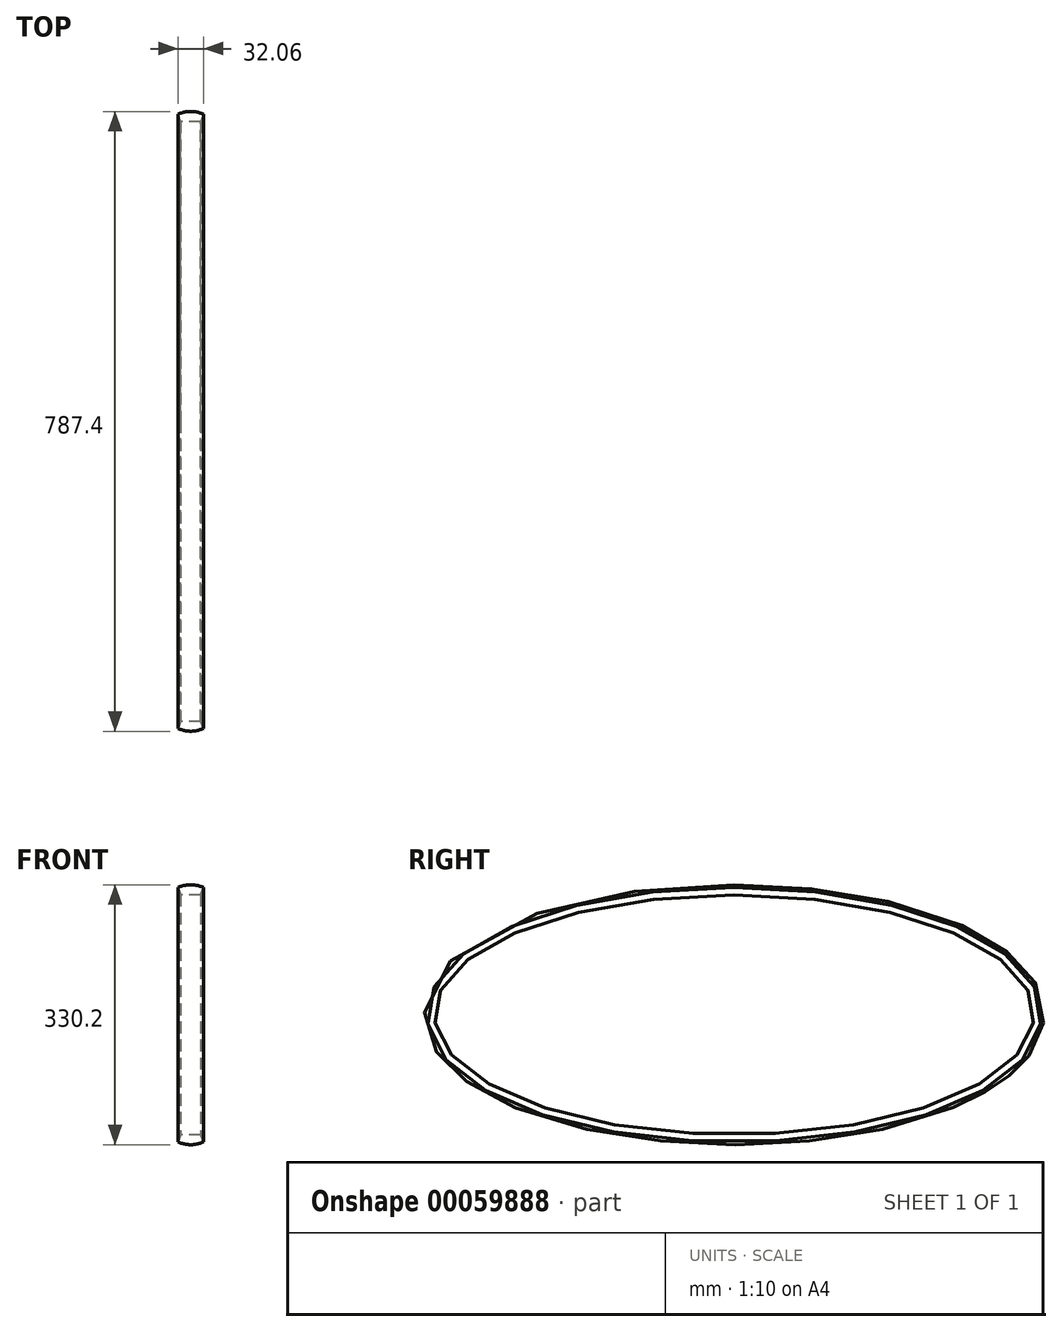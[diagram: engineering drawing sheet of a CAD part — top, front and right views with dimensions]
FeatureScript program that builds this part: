
annotation { "Feature Type Name" : "Feature", "Feature Type Description" : "" }
export const myFeature = defineFeature(function(context is Context, id is Id, definition is map)
    precondition{}
    {
        {
            var Q0;
            Q0=qCreatedBy(makeId("Front.planeOp"),FACE);
            var sketch = newSketch(context, id + "F0", { "sketchPlane" : qUnion([Q0])});
            skLineSegment(sketch, "E0", {"start": v(-12.7, 0) * mm, "end": v(12.7, 0) * mm});
            skLineSegment(sketch, "E1", {"start": v(12.7, 0) * mm, "end": v(16.03, 9.16) * mm});
            skLineSegment(sketch, "E2", {"start": v(-12.7, 0) * mm, "end": v(-16.03, 9.16) * mm});
            skArc(sketch, "E3", {"start": v(16.03, 9.16) * mm, "mid": v(0, 12.7) * mm, "end": v(-16.03, 9.16) * mm});
            skPoint(sketch, "E4", {"position": v(0, 0) * mm});
            skSolve(sketch);
        }
        {
            var Q0;
            Q0=qCreatedBy(makeId("Right.planeOp"),FACE);
            var sketch = newSketch(context, id + "F1", { "sketchPlane" : qUnion([Q0])});
            skEllipse(sketch, "E5", {"center": v(0, -152.4) * mm, "majorRadius": 381 * mm, "minorRadius": 152.4 * mm, "majorAxis": v(1, 0)});
            skSolve(sketch);
        }
        {
            var Q0;
            Q0 = qSketchRegion(id + "F0", true);
            var Q1;
            Q1 = qConstructionFilter(qBodyType(qCreatedBy(id + "F1" ,EDGE), BodyType.WIRE), ConstructionObject.NO);
            sweep(context, id + "F2", {"profiles" : qUnion([Q0]), "path" : qUnion([Q1])});
        }
    });
